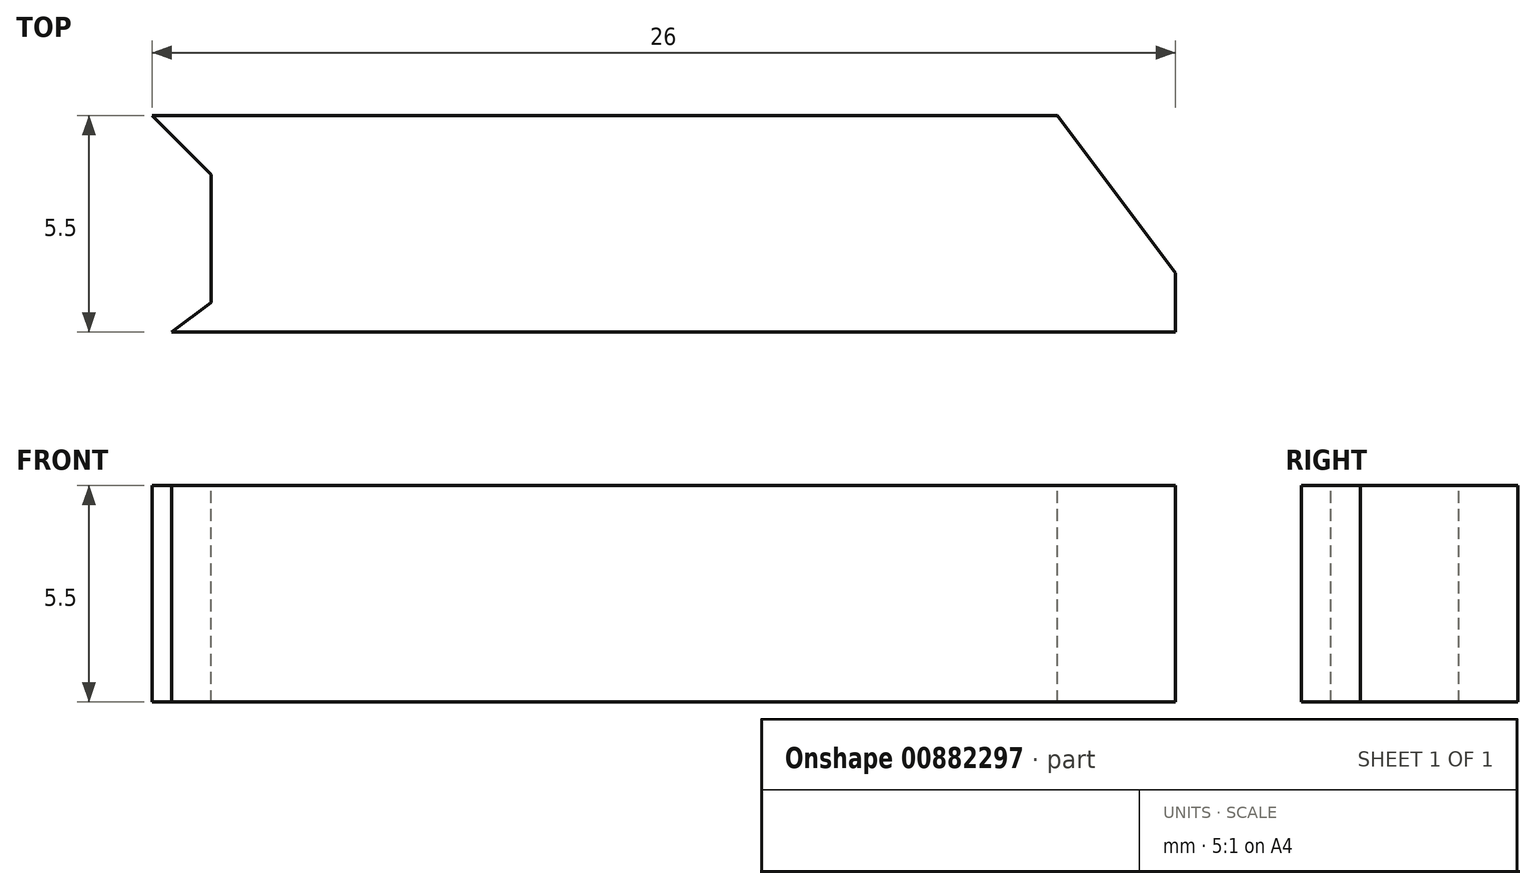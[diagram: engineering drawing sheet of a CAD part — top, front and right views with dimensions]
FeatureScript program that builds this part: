
annotation { "Feature Type Name" : "Feature", "Feature Type Description" : "" }
export const myFeature = defineFeature(function(context is Context, id is Id, definition is map)
    precondition{}
    {
        {
            var Q0;
            Q0=qCreatedBy(makeId("Right.planeOp"),FACE);
            var sketch = newSketch(context, id + "F0", { "sketchPlane" : qUnion([Q0])});
            skLineSegment(sketch, "E0.bottom", {"start": v(0, 0) * mm, "end": v(5.5, 0) * mm});
            skLineSegment(sketch, "E0.top", {"start": v(0, -5.5) * mm, "end": v(5.5, -5.5) * mm});
            skLineSegment(sketch, "E0.left", {"start": v(0, 0) * mm, "end": v(0, -5.5) * mm});
            skLineSegment(sketch, "E0.right", {"start": v(5.5, 0) * mm, "end": v(5.5, -5.5) * mm});
            skSolve(sketch);
        }
        {
            var Q0;
            Q0=makeQuery(id+"F0.imprint","IMPRINT",FACE,{"disambiguationData":[TD([[makeQuery(id+"F0.imprint","IMPRINT",EDGE,{"derivedFrom":sQuery(id+"F0.wireOp",EDGE,"E0.bottom")}),-1.0]])]});
            extrude(context, id + "F1", {"entities" : qUnion([Q0]), "endBound" : BoundingType.SYMMETRIC, "depth" : 26 * mm, "offsetDistance" : 25 * mm});
        }
        {
            var Q0;
            Q0=makeQuery(id+"F1.opExtrude","SWEPT_FACE",FACE,{"disambiguationData":[OSD([sQuery(id+"F0.wireOp",EDGE,"E0.bottom")])]});
            var sketch = newSketch(context, id + "F2", { "sketchPlane" : qUnion([Q0])});
            skLineSegment(sketch, "E1", {"start": v(-13, 5.5) * mm, "end": v(-11.5, 4) * mm});
            skLineSegment(sketch, "E2", {"start": v(-11.5, 4) * mm, "end": v(-11.5, 0.75) * mm});
            skLineSegment(sketch, "E3", {"start": v(-11.5, 0.75) * mm, "end": v(-12.5, 0) * mm});
            skLineSegment(sketch, "E4", {"start": v(10, 5.5) * mm, "end": v(13, 1.5) * mm});
            skSolve(sketch);
        }
        {
            var Q0;
            Q0=makeQuery(id+"F2.imprint","IMPRINT",FACE,{"disambiguationData":[TD([[makeQuery(id+"F2.imprint","IMPRINT",EDGE,{"derivedFrom":sQuery(id+"F2.wireOp",EDGE,"E1")}),-1.0]])]});
            var Q1;
            {var subQ0=sQuery(id+"F2.wireOp",EDGE,"E4");Q1=makeQuery(id+"F2.imprint","IMPRINT",FACE,{"disambiguationData":[TD([[makeQuery(id+"F2.imprint","IMPRINT",EDGE,{"derivedFrom":subQ0}),1.0]])]});}
            extrude(context, id + "F3", {"entities" : qUnion([Q0, Q1]), "operationType" : NewBodyOperationType.REMOVE, "endBound" : BoundingType.THROUGH_ALL, "oppositeDirection" : true, "depth" : 25 * mm, "offsetDistance" : 25 * mm});
        }
    });
